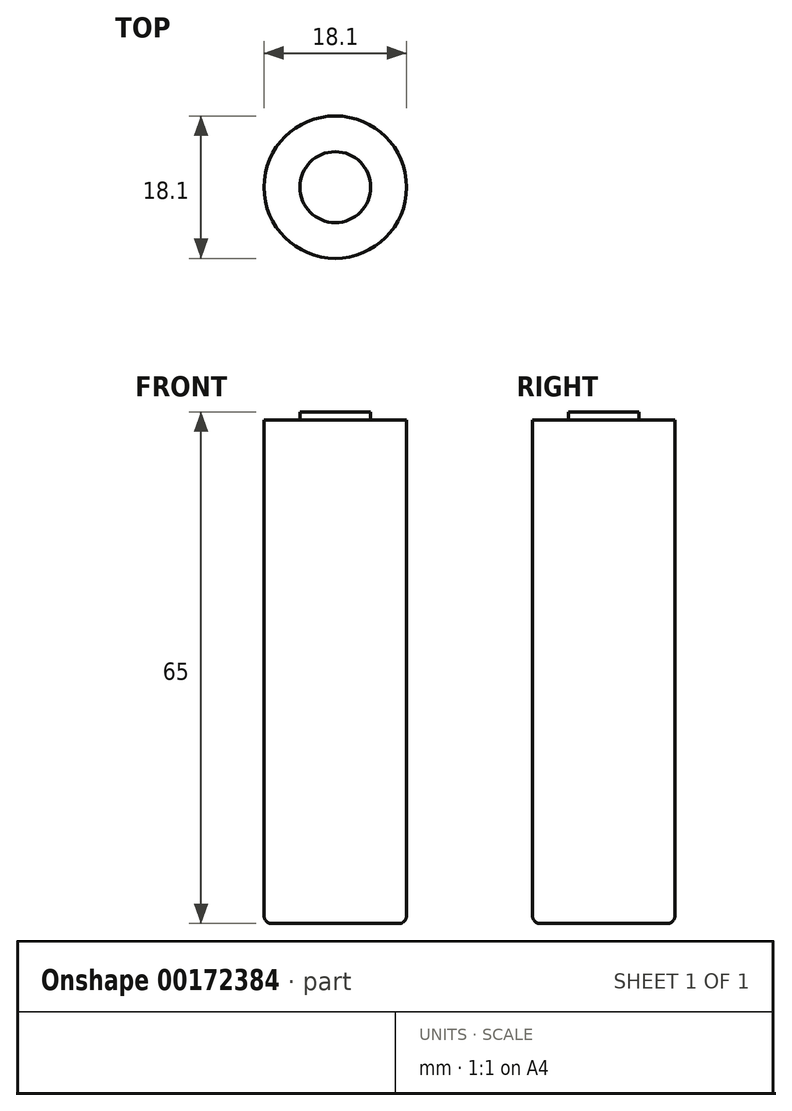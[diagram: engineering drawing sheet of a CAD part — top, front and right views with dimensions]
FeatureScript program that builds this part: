
annotation { "Feature Type Name" : "Feature", "Feature Type Description" : "" }
export const myFeature = defineFeature(function(context is Context, id is Id, definition is map)
    precondition{}
    {
        {
            var Q0;
            Q0=qCreatedBy(makeId("Top.planeOp"),FACE);
            var sketch = newSketch(context, id + "F0", { "sketchPlane" : qUnion([Q0])});
            skCircle(sketch, "E0", {"center": v(-32.21, -44.58) * mm, "radius": 9.05 * mm});
            skSolve(sketch);
        }
        {
            var Q0;
            Q0 = qSketchRegion(id + "F0", true);
            extrude(context, id + "F1", {"entities" : qUnion([Q0]), "depth" : 65 * mm});
        }
        {
            var Q0;
            Q0=makeQuery(id+"F1.opExtrude","CAP_FACE",FACE,{"disambiguationData":[OSD([sQuery(id+"F0.wireOp",EDGE,"E0")])],"isStart":false});
            var sketch = newSketch(context, id + "F2", { "sketchPlane" : qUnion([Q0])});
            skCircle(sketch, "E1", {"center": v(-32.21, -44.58) * mm, "radius": 4.5 * mm});
            skCircle(sketch, "E2", {"center": v(-32.21, -44.58) * mm, "radius": 9.05 * mm});
            skSolve(sketch);
        }
        {
            var Q0;
            Q0 = qSketchRegion(id + "F2", true);
            extrude(context, id + "F3", {"entities" : qUnion([Q0]), "operationType" : NewBodyOperationType.REMOVE, "oppositeDirection" : true, "depth" : 1 * mm});
        }
        {
            var Q0;
            Q0=makeQuery(id+"F3.boolean.opBoolean","COPY",EDGE,{"derivedFrom":makeQuery(id+"F3.opExtrude","CAP_EDGE",EDGE,{"disambiguationData":[OSD([sQuery(id+"F2.wireOp",EDGE,"E2")])],"isStart":false})});
            var Q1;
            Q1=makeQuery(id+"F1.opExtrude","CAP_EDGE",EDGE,{"disambiguationData":[OSD([sQuery(id+"F0.wireOp",EDGE,"E0")])],"isStart":true});
            fillet(context, id + "F4", {"entities" : qUnion([Q0, Q1]), "radius" : 1 * mm, "tangentPropagation" : true, "allowEdgeOverflow" : false});
        }
    });
